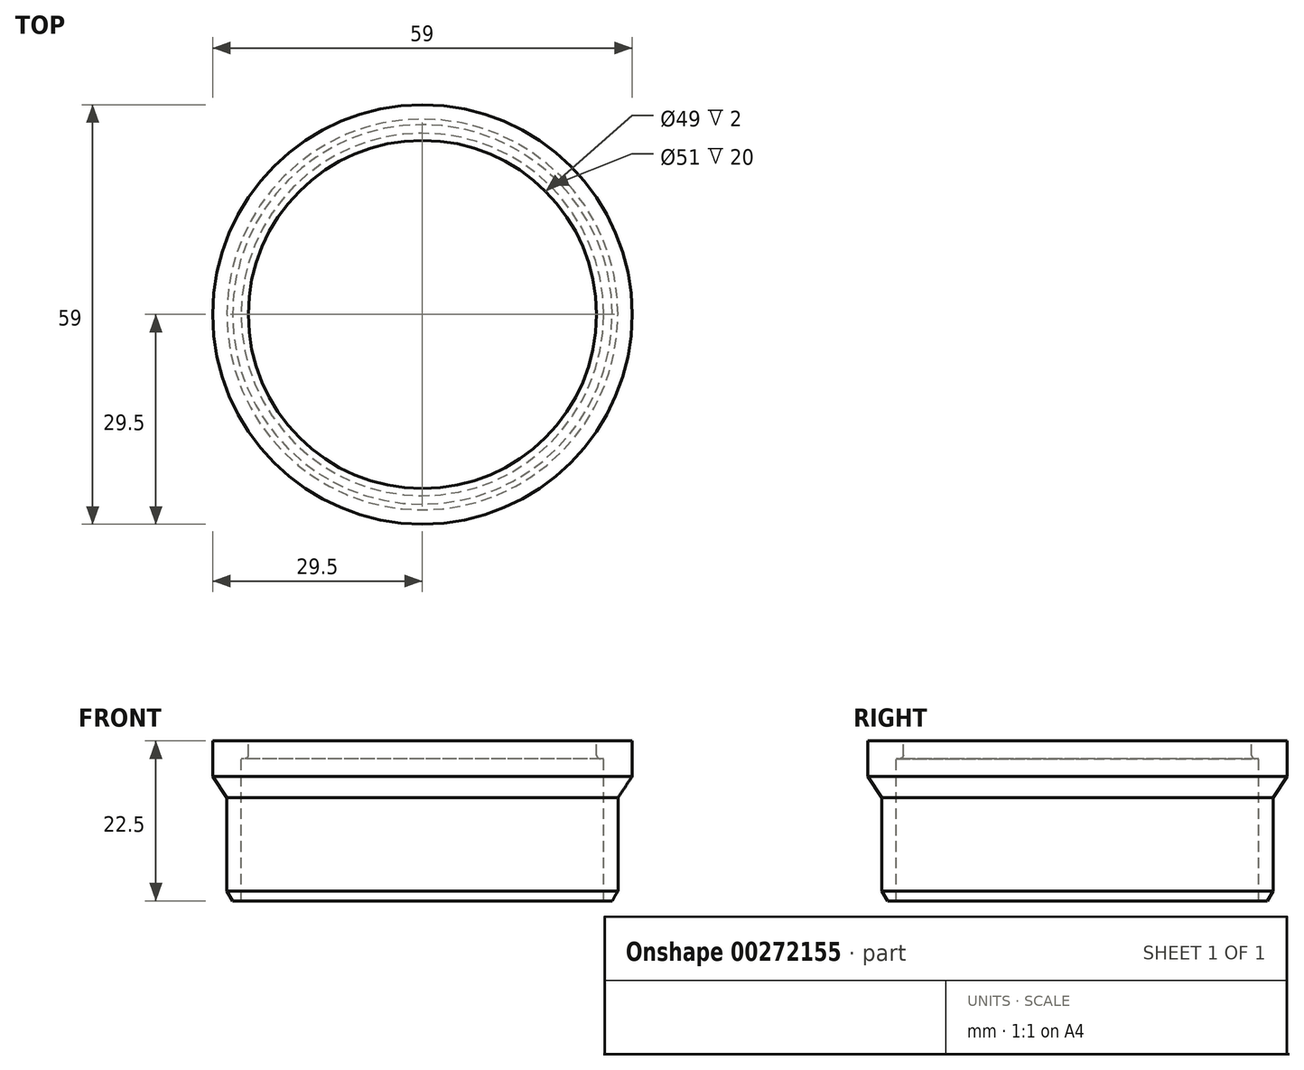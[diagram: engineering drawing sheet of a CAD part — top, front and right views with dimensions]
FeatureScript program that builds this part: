
annotation { "Feature Type Name" : "Feature", "Feature Type Description" : "" }
export const myFeature = defineFeature(function(context is Context, id is Id, definition is map)
    precondition{}
    {
        {
            var Q0;
            Q0=qCreatedBy(makeId("Front.planeOp"),FACE);
            var sketch = newSketch(context, id + "F0", { "sketchPlane" : qUnion([Q0])});
            skLineSegment(sketch, "E0", {"start": v(24.5, -12.87) * mm, "end": v(24.5, -14.87) * mm});
            skLineSegment(sketch, "E1", {"start": v(25.5, -15.37) * mm, "end": v(25, -15.37) * mm});
            skLineSegment(sketch, "E2", {"start": v(25.5, -15.37) * mm, "end": v(25.5, -35.37) * mm});
            skLineSegment(sketch, "E3", {"start": v(25.5, -35.37) * mm, "end": v(26.7, -35.37) * mm});
            skLineSegment(sketch, "E4", {"start": v(26.7, -35.37) * mm, "end": v(27.5, -33.98) * mm});
            skLineSegment(sketch, "E5", {"start": v(29.5, -17.87) * mm, "end": v(29.5, -12.87) * mm});
            skLineSegment(sketch, "E6", {"start": v(29.5, -12.87) * mm, "end": v(24.5, -12.87) * mm});
            skLineSegment(sketch, "E7", {"start": v(0, 24.42) * mm, "end": v(0, -13.18) * mm, "construction": true});
            skLineSegment(sketch, "E8", {"start": v(29.5, -17.87) * mm, "end": v(27.5, -20.87) * mm});
            skLineSegment(sketch, "E9", {"start": v(27.5, -20.87) * mm, "end": v(27.5, -33.98) * mm});
            skPoint(sketch, "E10.visualSharp", {"position": v(24.5, -15.37) * mm});
            skArc(sketch, "E10.filletArc", {"start": v(24.5, -14.87) * mm, "mid": v(24.65, -15.22) * mm, "end": v(25, -15.37) * mm});
            skSolve(sketch);
        }
        {
            var Q0;
            Q0=makeQuery(id+"F0.imprint","IMPRINT",FACE,{"disambiguationData":[TD([[makeQuery(id+"F0.imprint","IMPRINT",EDGE,{"derivedFrom":sQuery(id+"F0.wireOp",EDGE,"E0")}),1.0]])]});
            var Q1;
            Q1=sQuery(id+"F0.wireOp",EDGE,"E7");
            revolve(context, id + "F1", {"entities" : qUnion([Q0]), "axis" : qUnion([Q1]), "revolveType" : RevolveType.FULL});
        }
    });
